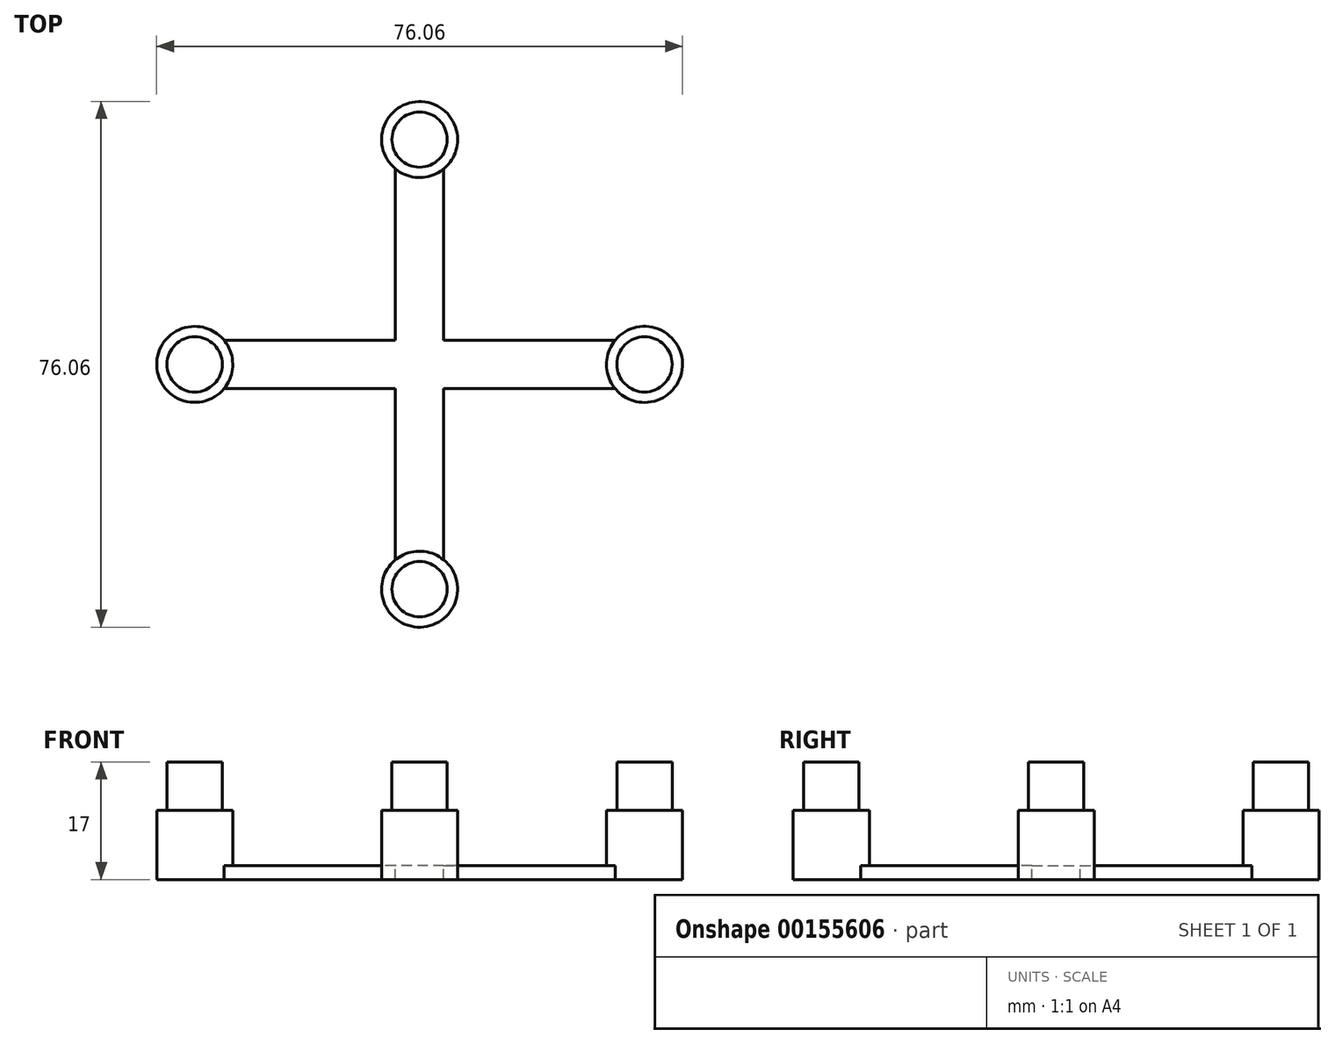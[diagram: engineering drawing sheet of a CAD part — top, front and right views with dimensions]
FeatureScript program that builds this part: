
annotation { "Feature Type Name" : "Feature", "Feature Type Description" : "" }
export const myFeature = defineFeature(function(context is Context, id is Id, definition is map)
    precondition{}
    {
        {
            var Q0;
            Q0=qCreatedBy(makeId("Top.planeOp"),FACE);
            var sketch = newSketch(context, id + "F0", { "sketchPlane" : qUnion([Q0])});
            skLineSegment(sketch, "E0.bottom", {"start": v(0, 0) * mm, "end": v(7, 0) * mm});
            skLineSegment(sketch, "E0.top", {"start": v(0, 32.53) * mm, "end": v(7, 32.53) * mm});
            skLineSegment(sketch, "E0.left", {"start": v(0, 0) * mm, "end": v(0, 32.53) * mm});
            skLineSegment(sketch, "E0.right", {"start": v(7, 0) * mm, "end": v(7, 32.53) * mm});
            skCircle(sketch, "E1", {"center": v(3.5, 32.53) * mm, "radius": 5.5 * mm});
            skCircle(sketch, "E2", {"center": v(3.5, 32.53) * mm, "radius": 4 * mm});
            skPoint(sketch, "E3", {"position": v(3.5, 0) * mm});
            skLineSegment(sketch, "E4", {"start": v(3.5, 32.53) * mm, "end": v(3.5, 0) * mm, "construction": true});
            skLineSegment(sketch, "E5", {"start": v(3.5, 32.53) * mm, "end": v(-29.03, 0) * mm, "construction": true});
            skSolve(sketch);
        }
        {
            var Q0;
            {var subQ0=sQuery(id+"F0.wireOp",EDGE,"E0.bottom");Q0=makeQuery(id+"F0.imprint","IMPRINT",FACE,{"disambiguationData":[TD([[makeQuery(id+"F0.imprint","IMPRINT",EDGE,{"derivedFrom":subQ0}),1.0]])]});}
            extrude(context, id + "F1", {"entities" : qUnion([Q0]), "depth" : 2 * mm});
        }
        {
            var Q0;
            {var subQ0=sQuery(id+"F0.wireOp",EDGE,"E1");var subQ1=sQuery(id+"F0.wireOp",EDGE,"E0.left");var subQ2=makeQuery(id+"F0.imprint","INTERSECT",VERTEX,{"derivedFrom":[subQ1,subQ0]});Q0=makeQuery(id+"F0.imprint","IMPRINT",FACE,{"disambiguationData":[TD([[makeQuery(id+"F0.imprint","IMPRINT",EDGE,{"disambiguationData":[TD([[subQ2,-1.0]])],"derivedFrom":subQ1}),1.0]])]});}
            var Q1;
            {var subQ0=sQuery(id+"F0.wireOp",EDGE,"E1");var subQ1=sQuery(id+"F0.wireOp",EDGE,"E0.left");var subQ2=makeQuery(id+"F0.imprint","INTERSECT",VERTEX,{"derivedFrom":[subQ1,subQ0]});Q1=makeQuery(id+"F0.imprint","IMPRINT",FACE,{"disambiguationData":[TD([[makeQuery(id+"F0.imprint","IMPRINT",EDGE,{"disambiguationData":[TD([[subQ2,-1.0]])],"derivedFrom":subQ1}),-1.0]])]});}
            extrude(context, id + "F2", {"entities" : qUnion([Q0, Q1]), "operationType" : NewBodyOperationType.ADD, "depth" : 10 * mm});
        }
        {
            var Q0;
            {var subQ0=sQuery(id+"F0.wireOp",EDGE,"E0.top");Q0=makeQuery(id+"F0.imprint","IMPRINT",FACE,{"disambiguationData":[TD([[makeQuery(id+"F0.imprint","IMPRINT",EDGE,{"derivedFrom":subQ0}),1.0]])]});}
            var Q1;
            {var subQ0=sQuery(id+"F0.wireOp",EDGE,"E0.top");Q1=makeQuery(id+"F0.imprint","IMPRINT",FACE,{"disambiguationData":[TD([[makeQuery(id+"F0.imprint","IMPRINT",EDGE,{"derivedFrom":subQ0}),-1.0]])]});}
            extrude(context, id + "F3", {"entities" : qUnion([Q0, Q1]), "operationType" : NewBodyOperationType.ADD, "depth" : 10 * mm + 7 * mm});
        }
        {
            var Q0;
            Q0=qCreatedBy(makeId("Right.planeOp"),FACE);
            var Q1;
            Q1=sQuery(id+"F0.wireOp",VERTEX,"E3");
            cPlane(context, id + "F4", {"entities" : qUnion([Q0, Q1]), "cplaneType" : CPlaneType.PLANE_POINT, "offset" : 25 * mm, "width" : 150 * mm, "height" : 150 * mm});
        }
        {
            var Q0;
            Q0=qCreatedBy(id+"F4.planeOp",FACE);
            var sketch = newSketch(context, id + "F5", { "sketchPlane" : qUnion([Q0])});
            skLineSegment(sketch, "E6", {"start": v(0, 0) * mm, "end": v(0, 42.38) * mm, "construction": true});
            skSolve(sketch);
        }
        {
            var Q0;
            Q0=makeQuery(id+"F1.opExtrude","SWEPT_BODY",BODY,{"disambiguationData":[OSD([sQuery(id+"F0.wireOp",EDGE,"E0.bottom"),sQuery(id+"F0.wireOp",EDGE,"E0.left"),sQuery(id+"F0.wireOp",EDGE,"E0.right"),sQuery(id+"F0.wireOp",EDGE,"E1")])]});
            var Q1;
            Q1=sQuery(id+"F5.wireOp",EDGE,"E6");
            circularPattern(context, id + "F6", {"operationType" : NewBodyOperationType.ADD, "entities" : qUnion([Q0]), "axis" : qUnion([Q1]), "angle" : 360 * degree, "instanceCount" : 4, "equalSpace" : true});
        }
    });
